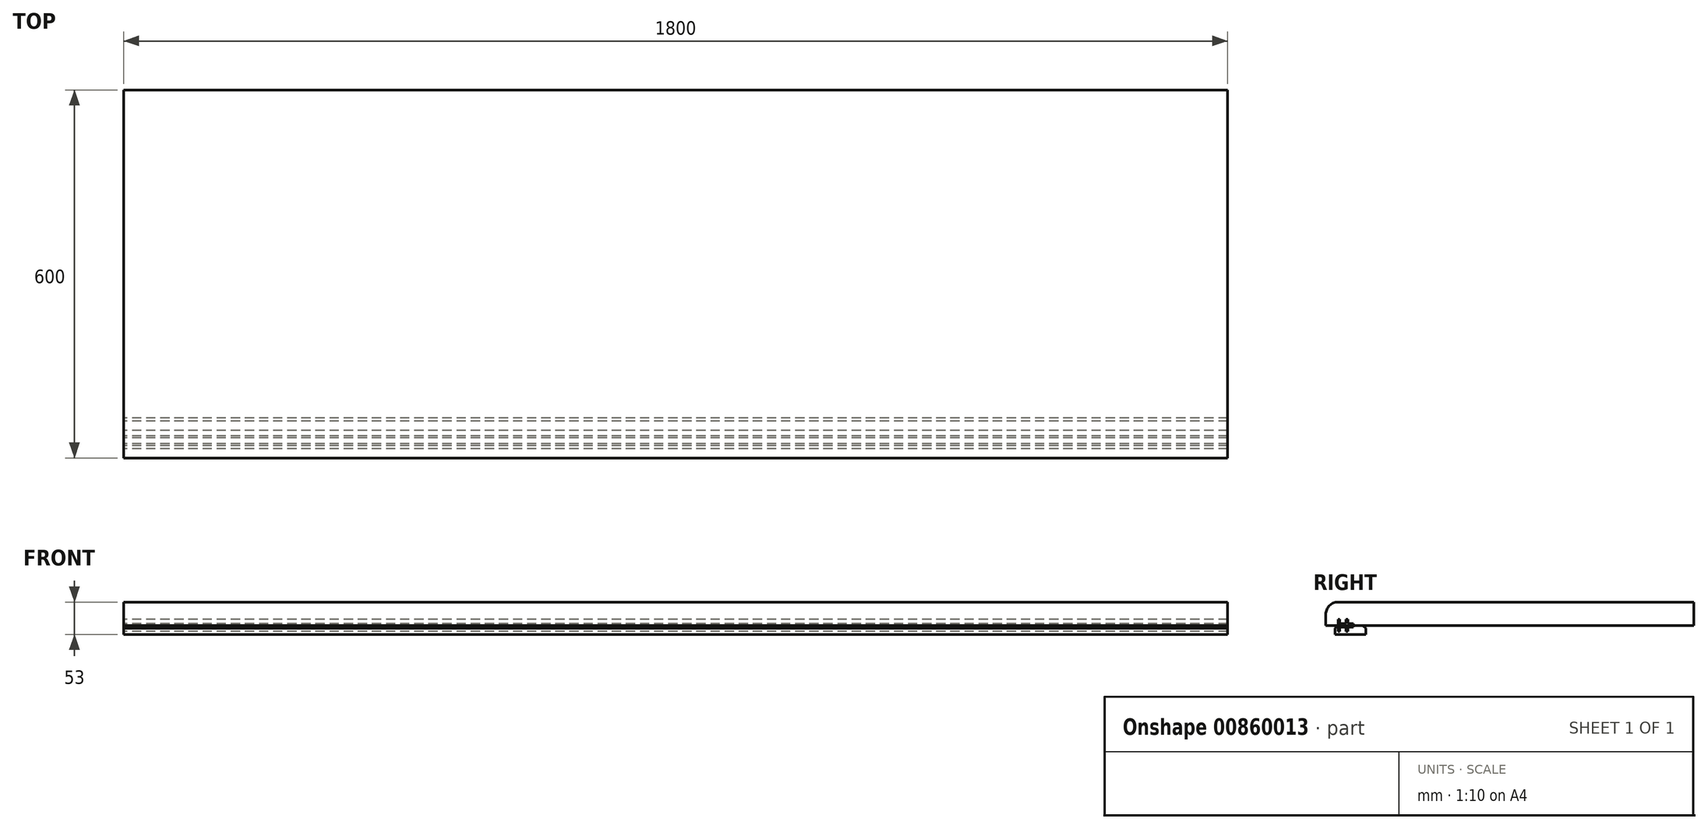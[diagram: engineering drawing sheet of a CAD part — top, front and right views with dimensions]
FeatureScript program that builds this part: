
annotation { "Feature Type Name" : "Feature", "Feature Type Description" : "" }
export const myFeature = defineFeature(function(context is Context, id is Id, definition is map)
    precondition{}
    {
        {
            var Q0;
            Q0=qCreatedBy(makeId("Right.planeOp"),FACE);
            var sketch = newSketch(context, id + "F0", { "sketchPlane" : qUnion([Q0])});
            skLineSegment(sketch, "E0", {"start": v(-20, 0) * mm, "end": v(580, 0) * mm});
            skLineSegment(sketch, "E1", {"start": v(580, 0) * mm, "end": v(580, 38) * mm});
            skLineSegment(sketch, "E2", {"start": v(580, 38) * mm, "end": v(0, 38) * mm});
            skLineSegment(sketch, "E3", {"start": v(-20, 18) * mm, "end": v(-20, 0) * mm});
            skPoint(sketch, "E4.visualSharp", {"position": v(-20, 38) * mm});
            skArc(sketch, "E4.filletArc", {"start": v(0, 38) * mm, "mid": v(-14.14, 32.14) * mm, "end": v(-20, 18) * mm});
            skSolve(sketch);
        }
        {
            var Q0;
            Q0=makeQuery(id+"F0.imprint","IMPRINT",FACE,{"disambiguationData":[TD([[makeQuery(id+"F0.imprint","IMPRINT",EDGE,{"derivedFrom":sQuery(id+"F0.wireOp",EDGE,"E0")}),1.0]])]});
            extrude(context, id + "F1", {"entities" : qUnion([Q0]), "depth" : 1800 * mm, "offsetDistance" : 25 * mm, "symmetric" : true});
        }
        {
            var Q0;
            Q0=qCreatedBy(makeId("Right.planeOp"),FACE);
            var sketch = newSketch(context, id + "F2", { "sketchPlane" : qUnion([Q0])});
            skLineSegment(sketch, "E5", {"start": v(0, 0) * mm, "end": v(25, 0) * mm});
            skLineSegment(sketch, "E6", {"start": v(0, 0) * mm, "end": v(0, 10) * mm});
            skLineSegment(sketch, "E7", {"start": v(0, 10) * mm, "end": v(3, 10) * mm});
            skLineSegment(sketch, "E8", {"start": v(25, 0) * mm, "end": v(25, 3) * mm});
            skLineSegment(sketch, "E9", {"start": v(13, 3) * mm, "end": v(3, 3) * mm});
            skLineSegment(sketch, "E10", {"start": v(3, 10) * mm, "end": v(3, 3) * mm});
            skLineSegment(sketch, "E11", {"start": v(13, 10) * mm, "end": v(13, 3) * mm});
            skLineSegment(sketch, "E12", {"start": v(16, 10) * mm, "end": v(16, 3) * mm});
            skLineSegment(sketch, "E13", {"start": v(13, 10) * mm, "end": v(16, 10) * mm});
            skLineSegment(sketch, "E14", {"start": v(16, 3) * mm, "end": v(25, 3) * mm});
            skSolve(sketch);
        }
        {
            var Q0;
            Q0=makeQuery(id+"F2.imprint","IMPRINT",FACE,{"disambiguationData":[TD([[makeQuery(id+"F2.imprint","IMPRINT",EDGE,{"derivedFrom":sQuery(id+"F2.wireOp",EDGE,"E5")}),1.0]])]});
            extrude(context, id + "F3", {"entities" : qUnion([Q0]), "depth" : 1800 * mm, "offsetDistance" : 25 * mm, "symmetric" : true});
        }
        {
            var Q0;
            Q0=qCreatedBy(makeId("Right.planeOp"),FACE);
            var sketch = newSketch(context, id + "F4", { "sketchPlane" : qUnion([Q0])});
            skLineSegment(sketch, "E15.0", {"start": v(0, 0) * mm, "end": v(25, 0) * mm});
            skLineSegment(sketch, "E16", {"start": v(0, 0) * mm, "end": v(-5, -5) * mm});
            skLineSegment(sketch, "E17", {"start": v(-5, -5) * mm, "end": v(-5, -15) * mm});
            skLineSegment(sketch, "E18", {"start": v(-5, -15) * mm, "end": v(45, -15) * mm});
            skLineSegment(sketch, "E19", {"start": v(45, -15) * mm, "end": v(45, -5) * mm});
            skLineSegment(sketch, "E20", {"start": v(45, -5) * mm, "end": v(40, 0) * mm});
            skLineSegment(sketch, "E21", {"start": v(40, 0) * mm, "end": v(25, 0) * mm});
            skSolve(sketch);
        }
        {
            var Q0;
            Q0=makeQuery(id+"F4.imprint","IMPRINT",FACE,{"disambiguationData":[TD([[makeQuery(id+"F4.imprint","IMPRINT",EDGE,{"derivedFrom":sQuery(id+"F4.wireOp",EDGE,"E15.0")}),-1.0]])]});
            extrude(context, id + "F5", {"entities" : qUnion([Q0]), "depth" : 1800 * mm, "offsetDistance" : 25 * mm, "symmetric" : true});
        }
        {
            var Q0;
            Q0=qCreatedBy(makeId("Right.planeOp"),FACE);
            var sketch = newSketch(context, id + "F6", { "sketchPlane" : qUnion([Q0])});
            skLineSegment(sketch, "E22.0", {"start": v(0, 0) * mm, "end": v(25, 0) * mm});
            skLineSegment(sketch, "E23", {"start": v(0, 0) * mm, "end": v(0, -10) * mm});
            skLineSegment(sketch, "E24", {"start": v(0, -10) * mm, "end": v(3, -10) * mm});
            skLineSegment(sketch, "E25", {"start": v(3, -3) * mm, "end": v(13, -3) * mm});
            skLineSegment(sketch, "E26", {"start": v(16, -3) * mm, "end": v(25, -3) * mm});
            skLineSegment(sketch, "E27", {"start": v(3, -3) * mm, "end": v(3, -10) * mm});
            skLineSegment(sketch, "E28", {"start": v(13, -3) * mm, "end": v(13, -10) * mm});
            skLineSegment(sketch, "E29", {"start": v(16, -3) * mm, "end": v(16, -10) * mm});
            skLineSegment(sketch, "E30", {"start": v(25, 0) * mm, "end": v(25, -3) * mm});
            skLineSegment(sketch, "E31", {"start": v(13, -10) * mm, "end": v(16, -10) * mm});
            skSolve(sketch);
        }
        {
            var Q0;
            Q0=makeQuery(id+"F6.imprint","IMPRINT",FACE,{"disambiguationData":[TD([[makeQuery(id+"F6.imprint","IMPRINT",EDGE,{"derivedFrom":sQuery(id+"F6.wireOp",EDGE,"E22.0")}),-1.0]])]});
            extrude(context, id + "F7", {"entities" : qUnion([Q0]), "depth" : 1800 * mm, "offsetDistance" : 25 * mm, "symmetric" : true});
        }
    });
